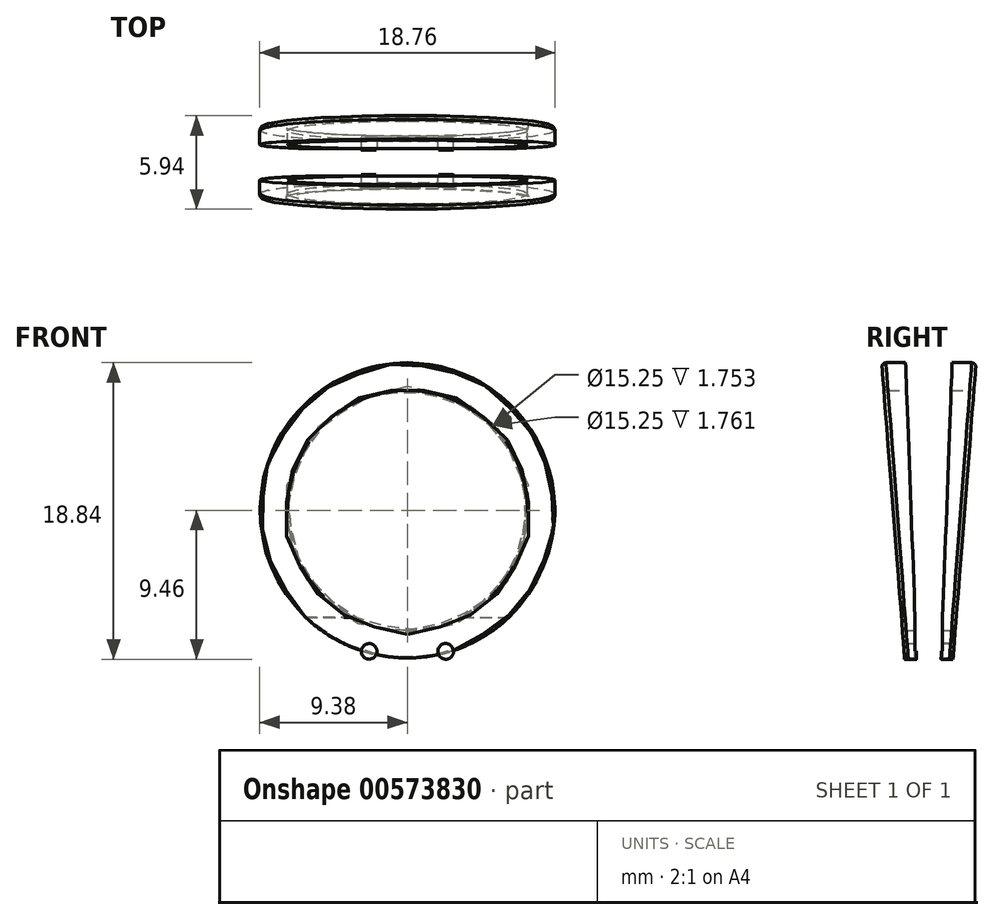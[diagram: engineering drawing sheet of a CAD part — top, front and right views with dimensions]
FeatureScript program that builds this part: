
annotation { "Feature Type Name" : "Feature", "Feature Type Description" : "" }
export const myFeature = defineFeature(function(context is Context, id is Id, definition is map)
    precondition{}
    {
        {
            var Q0;
            Q0=qCreatedBy(makeId("Front.planeOp"),FACE);
            var sketch = newSketch(context, id + "F0", { "sketchPlane" : qUnion([Q0])});
            skCircle(sketch, "E0", {"center": v(0, 0) * mm, "radius": 7.62 * mm});
            skCircle(sketch, "E1", {"center": v(0, 0) * mm, "radius": 9.38 * mm});
            skSolve(sketch);
        }
        {
            var Q0;
            Q0 = qSketchRegion(id + "F0", true);
            extrude(context, id + "F1", {"entities" : qUnion([Q0]), "endBound" : BoundingType.SYMMETRIC, "depth" : 10 * mm, "offsetDistance" : 25 * mm});
        }
        {
            var Q0;
            Q0=qCreatedBy(makeId("Right.planeOp"),FACE);
            var sketch = newSketch(context, id + "F2", { "sketchPlane" : qUnion([Q0])});
            skLineSegment(sketch, "E2", {"start": v(-1.5, 19.04) * mm, "end": v(-1.5, 7.07) * mm});
            skLineSegment(sketch, "E3", {"start": v(-0.75, -19.02) * mm, "end": v(-0.75, -6.37) * mm});
            skSolve(sketch);
        }
        {
            var Q0;
            Q0=qCreatedBy(makeId("Right.planeOp"),FACE);
            var sketch = newSketch(context, id + "F3", { "sketchPlane" : qUnion([Q0])});
            skLineSegment(sketch, "E4", {"start": v(-1.9, 20.69) * mm, "end": v(-0.69, -11.82) * mm});
            skLineSegment(sketch, "E5", {"start": v(-0.69, -11.82) * mm, "end": v(0, -11.8) * mm});
            skLineSegment(sketch, "E6", {"start": v(0, -11.8) * mm, "end": v(0, 20.45) * mm});
            skLineSegment(sketch, "E7", {"start": v(0, 20.45) * mm, "end": v(-1.9, 20.69) * mm});
            skLineSegment(sketch, "E8.MirrorCS", {"start": v(1.9, 20.69) * mm, "end": v(0.69, -11.82) * mm});
            skLineSegment(sketch, "E9.MirrorCS", {"start": v(0, 20.45) * mm, "end": v(1.9, 20.69) * mm});
            skLineSegment(sketch, "E10.MirrorCS", {"start": v(0.69, -11.82) * mm, "end": v(0, -11.8) * mm});
            skSolve(sketch);
        }
        {
            var Q0;
            Q0=qCreatedBy(makeId("Right.planeOp"),FACE);
            var sketch = newSketch(context, id + "F4", { "sketchPlane" : qUnion([Q0])});
            skLineSegment(sketch, "E11", {"start": v(-3.25, 12.74) * mm, "end": v(-1.34, -11.97) * mm});
            skLineSegment(sketch, "E12", {"start": v(-1.34, -11.97) * mm, "end": v(-7.15, -11.97) * mm});
            skLineSegment(sketch, "E13", {"start": v(-7.15, -11.97) * mm, "end": v(-7.15, 12.74) * mm});
            skLineSegment(sketch, "E14", {"start": v(-7.15, 12.74) * mm, "end": v(-3.25, 12.74) * mm});
            skLineSegment(sketch, "E15.MirrorCS", {"start": v(7.15, 12.74) * mm, "end": v(3.25, 12.74) * mm});
            skLineSegment(sketch, "E16.MirrorCS", {"start": v(3.25, 12.74) * mm, "end": v(1.34, -11.97) * mm});
            skLineSegment(sketch, "E17.MirrorCS", {"start": v(7.15, -11.97) * mm, "end": v(7.15, 12.74) * mm});
            skLineSegment(sketch, "E18.MirrorCS", {"start": v(1.34, -11.97) * mm, "end": v(7.15, -11.97) * mm});
            skSolve(sketch);
        }
        {
            var Q0;
            Q0=qCreatedBy(makeId("Top.planeOp"),FACE);
            cPlane(context, id + "F5", {"entities" : qUnion([Q0]), "cplaneType" : CPlaneType.OFFSET, "offset" : 8.96 * mm, "oppositeDirection" : true, "width" : 150 * mm, "height" : 150 * mm});
        }
        {
            var Q0;
            Q0=qCreatedBy(makeId("Front.planeOp"),FACE);
            var sketch = newSketch(context, id + "F6", { "sketchPlane" : qUnion([Q0])});
            skCircle(sketch, "E19", {"center": v(0, 0) * mm, "radius": 9.38 * mm});
            skSolve(sketch);
        }
        {
            var Q0;
            Q0=qCreatedBy(id+"F5.planeOp",FACE);
            var sketch = newSketch(context, id + "F7", { "sketchPlane" : qUnion([Q0])});
            skLineSegment(sketch, "E20", {"start": v(-2.93, -6) * mm, "end": v(-2.93, 5.84) * mm});
            skLineSegment(sketch, "E21", {"start": v(-2.93, 5.84) * mm, "end": v(-1.93, 5.84) * mm});
            skLineSegment(sketch, "E22", {"start": v(-1.93, 5.84) * mm, "end": v(-1.93, -6) * mm});
            skLineSegment(sketch, "E23", {"start": v(-1.93, -6) * mm, "end": v(-2.93, -6) * mm});
            skLineSegment(sketch, "E24.MirrorCS", {"start": v(1.93, -6) * mm, "end": v(2.93, -6) * mm});
            skLineSegment(sketch, "E25.MirrorCS", {"start": v(2.93, -6) * mm, "end": v(2.93, 5.84) * mm});
            skLineSegment(sketch, "E26.MirrorCS", {"start": v(1.93, 5.84) * mm, "end": v(1.93, -6) * mm});
            skLineSegment(sketch, "E27.MirrorCS", {"start": v(2.93, 5.84) * mm, "end": v(1.93, 5.84) * mm});
            skPoint(sketch, "E28", {"position": v(-2.43, -6) * mm});
            skLineSegment(sketch, "E29", {"start": v(-2.43, -6) * mm, "end": v(-2.43, 5.84) * mm});
            skLineSegment(sketch, "E30", {"start": v(2.43, 5.84) * mm, "end": v(2.43, -6) * mm});
            skSolve(sketch);
        }
        {
            var Q0;
            {var subQ0=sQuery(id+"F7.wireOp",EDGE,"E26.MirrorCS");Q0=makeQuery(id+"F7.imprint","IMPRINT",FACE,{"disambiguationData":[TD([[makeQuery(id+"F7.imprint","IMPRINT",EDGE,{"derivedFrom":subQ0}),1.0]])]});}
            var Q1;
            Q1=sQuery(id+"F7.wireOp",EDGE,"E30");
            revolve(context, id + "F8", {"entities" : qUnion([Q0]), "axis" : qUnion([Q1]), "revolveType" : RevolveType.FULL});
        }
        {
            var Q0;
            {var subQ0=sQuery(id+"F7.wireOp",EDGE,"E20");Q0=makeQuery(id+"F7.imprint","IMPRINT",FACE,{"disambiguationData":[TD([[makeQuery(id+"F7.imprint","IMPRINT",EDGE,{"derivedFrom":subQ0}),-1.0]])]});}
            var Q1;
            Q1=sQuery(id+"F7.wireOp",EDGE,"E29");
            revolve(context, id + "F9", {"entities" : qUnion([Q0]), "axis" : qUnion([Q1]), "revolveType" : RevolveType.FULL});
        }
        {
            var Q0;
            Q0 = qSketchRegion(id + "F3", true);
            extrude(context, id + "F10", {"entities" : qUnion([Q0]), "operationType" : NewBodyOperationType.REMOVE, "endBound" : BoundingType.SYMMETRIC, "oppositeDirection" : true, "depth" : 25 * mm, "offsetDistance" : 25 * mm});
        }
        {
            var Q0;
            Q0 = qSketchRegion(id + "F4", true);
            extrude(context, id + "F11", {"entities" : qUnion([Q0]), "operationType" : NewBodyOperationType.REMOVE, "endBound" : BoundingType.SYMMETRIC, "oppositeDirection" : true, "depth" : 25 * mm, "offsetDistance" : 25 * mm});
        }
        {
            var Q0;
            Q0 = qSketchRegion(id + "F6", true);
            extrude(context, id + "F12", {"entities" : qUnion([Q0]), "endBound" : BoundingType.SYMMETRIC, "depth" : 1.65 * mm, "offsetDistance" : 25 * mm});
        }
        {
            var Q0;
            Q0 = qSketchRegion(id + "F6", true);
            extrude(context, id + "F13", {"entities" : qUnion([Q0]), "operationType" : NewBodyOperationType.REMOVE, "endBound" : BoundingType.SYMMETRIC, "depth" : 1.75 * mm, "offsetDistance" : 25 * mm});
        }
        {
            var Q0;
            {var subQ0=sQuery(id+"F0.wireOp",EDGE,"E1");Q0=makeQuery(id+"F11.boolean.opBoolean","INTERSECT",EDGE,{"derivedFrom":[makeQuery(id+"FOoFwPogXX64BZm_1.boolean.opBoolean","SPLIT",FACE,{"disambiguationData":[OD(0.0)],"derivedFrom":makeQuery(id+"F10.boolean.opBoolean","SPLIT",FACE,{"disambiguationData":[TD([makeQuery(id+"F10.opExtrude","SWEPT_FACE",FACE,{"disambiguationData":[OSD([sQuery(id+"F3.wireOp",EDGE,"E4")])]})])],"derivedFrom":makeQuery(id+"F1.opExtrude","SWEPT_FACE",FACE,{"disambiguationData":[OSD([subQ0])]})})}),makeQuery(id+"F11.opExtrude","SWEPT_FACE",FACE,{"disambiguationData":[OSD([sQuery(id+"F4.wireOp",EDGE,"E11")])]})]});}
            var Q1;
            {var subQ0=sQuery(id+"F0.wireOp",EDGE,"E1");Q1=makeQuery(id+"F11.boolean.opBoolean","INTERSECT",EDGE,{"derivedFrom":[makeQuery(id+"FOoFwPogXX64BZm_1.boolean.opBoolean","SPLIT",FACE,{"disambiguationData":[OD(0.0)],"derivedFrom":makeQuery(id+"F10.boolean.opBoolean","SPLIT",FACE,{"disambiguationData":[TD([makeQuery(id+"F10.opExtrude","SWEPT_FACE",FACE,{"disambiguationData":[OSD([sQuery(id+"F3.wireOp",EDGE,"E8.MirrorCS")])]})])],"derivedFrom":makeQuery(id+"F1.opExtrude","SWEPT_FACE",FACE,{"disambiguationData":[OSD([subQ0])]})})}),makeQuery(id+"F11.opExtrude","SWEPT_FACE",FACE,{"disambiguationData":[OSD([sQuery(id+"F4.wireOp",EDGE,"E16.MirrorCS")])]})]});}
            var Q2;
            {var subQ0=sQuery(id+"F0.wireOp",EDGE,"E0");Q2=makeQuery(id+"F11.boolean.opBoolean","INTERSECT",EDGE,{"derivedFrom":[makeQuery(id+"F10.boolean.opBoolean","SPLIT",FACE,{"disambiguationData":[TD([makeQuery(id+"F10.opExtrude","SWEPT_FACE",FACE,{"disambiguationData":[OSD([sQuery(id+"F3.wireOp",EDGE,"E8.MirrorCS")])]})])],"derivedFrom":makeQuery(id+"F1.opExtrude","SWEPT_FACE",FACE,{"disambiguationData":[OSD([subQ0])]})}),makeQuery(id+"F11.opExtrude","SWEPT_FACE",FACE,{"disambiguationData":[OSD([sQuery(id+"F4.wireOp",EDGE,"E16.MirrorCS")])]})]});}
            var Q3;
            {var subQ0=sQuery(id+"F0.wireOp",EDGE,"E0");Q3=makeQuery(id+"F11.boolean.opBoolean","INTERSECT",EDGE,{"derivedFrom":[makeQuery(id+"F10.boolean.opBoolean","SPLIT",FACE,{"disambiguationData":[TD([makeQuery(id+"F10.opExtrude","SWEPT_FACE",FACE,{"disambiguationData":[OSD([sQuery(id+"F3.wireOp",EDGE,"E4")])]})])],"derivedFrom":makeQuery(id+"F1.opExtrude","SWEPT_FACE",FACE,{"disambiguationData":[OSD([subQ0])]})}),makeQuery(id+"F11.opExtrude","SWEPT_FACE",FACE,{"disambiguationData":[OSD([sQuery(id+"F4.wireOp",EDGE,"E11")])]})]});}
            var Q4;
            {var subQ0=sQuery(id+"F0.wireOp",EDGE,"E1");Q4=makeQuery(id+"F11.boolean.opBoolean","INTERSECT",EDGE,{"derivedFrom":[makeQuery(id+"FOoFwPogXX64BZm_1.boolean.opBoolean","SPLIT",FACE,{"disambiguationData":[OD(1.0)],"derivedFrom":makeQuery(id+"F10.boolean.opBoolean","SPLIT",FACE,{"disambiguationData":[TD([makeQuery(id+"F10.opExtrude","SWEPT_FACE",FACE,{"disambiguationData":[OSD([sQuery(id+"F3.wireOp",EDGE,"E8.MirrorCS")])]})])],"derivedFrom":makeQuery(id+"F1.opExtrude","SWEPT_FACE",FACE,{"disambiguationData":[OSD([subQ0])]})})}),makeQuery(id+"F11.opExtrude","SWEPT_FACE",FACE,{"disambiguationData":[OSD([sQuery(id+"F4.wireOp",EDGE,"E16.MirrorCS")])]})]});}
            var Q5;
            {var subQ0=sQuery(id+"F0.wireOp",EDGE,"E1");Q5=makeQuery(id+"F11.boolean.opBoolean","INTERSECT",EDGE,{"derivedFrom":[makeQuery(id+"FOoFwPogXX64BZm_1.boolean.opBoolean","SPLIT",FACE,{"disambiguationData":[OD(1.0)],"derivedFrom":makeQuery(id+"F10.boolean.opBoolean","SPLIT",FACE,{"disambiguationData":[TD([makeQuery(id+"F10.opExtrude","SWEPT_FACE",FACE,{"disambiguationData":[OSD([sQuery(id+"F3.wireOp",EDGE,"E4")])]})])],"derivedFrom":makeQuery(id+"F1.opExtrude","SWEPT_FACE",FACE,{"disambiguationData":[OSD([subQ0])]})})}),makeQuery(id+"F11.opExtrude","SWEPT_FACE",FACE,{"disambiguationData":[OSD([sQuery(id+"F4.wireOp",EDGE,"E11")])]})]});}
            fillet(context, id + "F14", {"entities" : qUnion([Q0, Q1, Q2, Q3, Q4, Q5]), "radius" : .25 * mm, "tangentPropagation" : true, "allowEdgeOverflow" : false});
        }
    });
